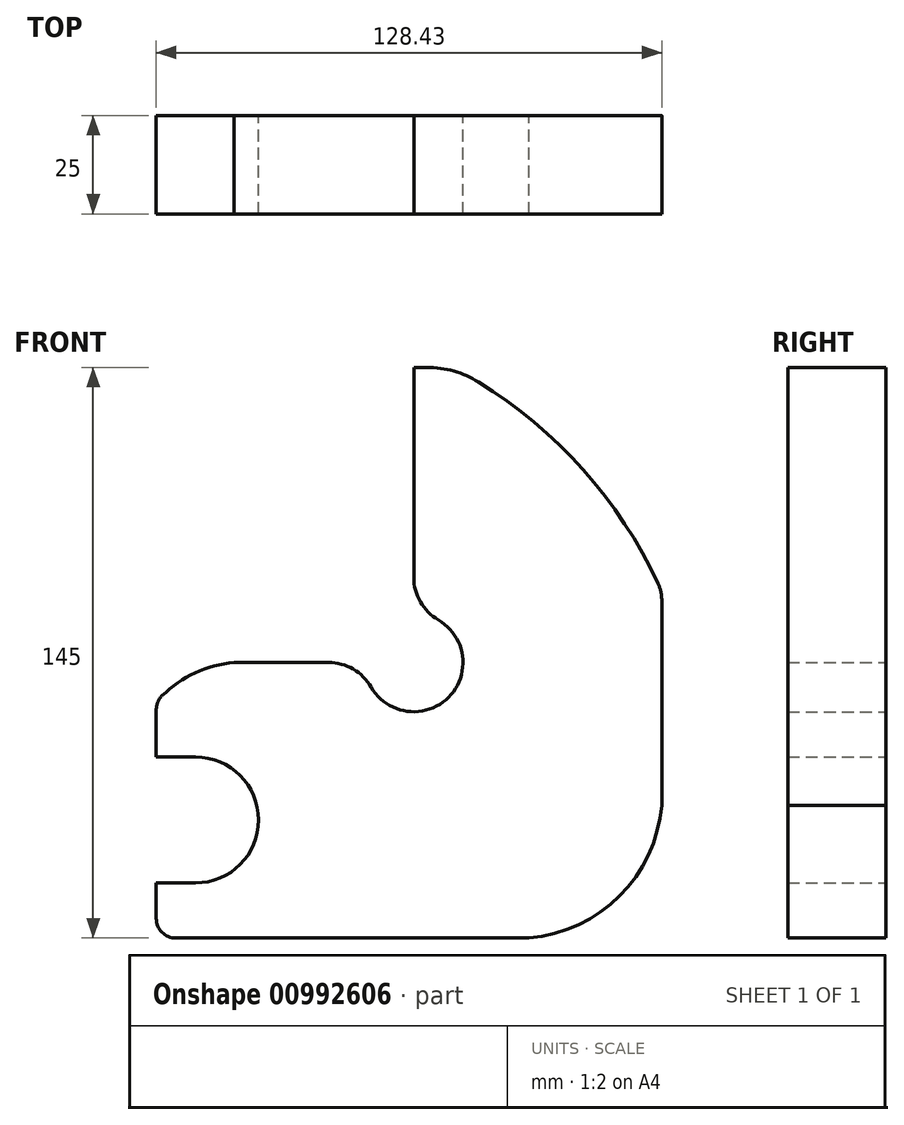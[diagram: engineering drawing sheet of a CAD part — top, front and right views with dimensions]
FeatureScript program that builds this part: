
annotation { "Feature Type Name" : "Feature", "Feature Type Description" : "" }
export const myFeature = defineFeature(function(context is Context, id is Id, definition is map)
    precondition{}
    {
        {
            var Q0;
            Q0=qCreatedBy(makeId("Front.planeOp"),FACE);
            var sketch = newSketch(context, id + "F0", { "sketchPlane" : qUnion([Q0])});
            skLineSegment(sketch, "E0", {"start": v(0, 0) * mm, "end": v(65.43, 0) * mm});
            skLineSegment(sketch, "E1", {"start": v(65.43, 0) * mm, "end": v(65.43, 75) * mm});
            skLineSegment(sketch, "E2", {"start": v(65.43, 75) * mm, "end": v(128.43, 75) * mm});
            skLineSegment(sketch, "E3", {"start": v(128.43, 75) * mm, "end": v(128.43, -70) * mm});
            skLineSegment(sketch, "E4", {"start": v(128.43, -70) * mm, "end": v(0, -70) * mm});
            skLineSegment(sketch, "E5", {"start": v(0, -70) * mm, "end": v(0, -56) * mm});
            skLineSegment(sketch, "E6", {"start": v(0, -24) * mm, "end": v(0, 0) * mm});
            skPoint(sketch, "E7", {"position": v(75.43, 75) * mm});
            skPoint(sketch, "E8", {"position": v(128.43, 18) * mm});
            skPoint(sketch, "E9", {"position": v(128.43, -30) * mm});
            skPoint(sketch, "E10", {"position": v(0, -10) * mm});
            skArc(sketch, "E11", {"start": v(128.43, 18) * mm, "mid": v(106.68, 50.92) * mm, "end": v(75.43, 75) * mm});
            skArc(sketch, "E12", {"start": v(88.43, -70) * mm, "mid": v(117.72, -59.3) * mm, "end": v(128.43, -30) * mm});
            skArc(sketch, "E13", {"start": v(25.22, 0) * mm, "mid": v(11.42, -1.99) * mm, "end": v(0, -10) * mm});
            skCircle(sketch, "E14", {"center": v(65.43, 0) * mm, "radius": 12.5 * mm});
            skCircle(sketch, "E15", {"center": v(10, -40) * mm, "radius": 16 * mm});
            skLineSegment(sketch, "E16", {"start": v(0, -56) * mm, "end": v(10, -56) * mm});
            skLineSegment(sketch, "E17", {"start": v(0, -24) * mm, "end": v(10, -24) * mm});
            skSolve(sketch);
        }
        {
            var Q0;
            {var subQ0=sQuery(id+"F0.wireOp",EDGE,"E5");Q0=makeQuery(id+"F0.imprint","IMPRINT",FACE,{"disambiguationData":[TD([[makeQuery(id+"F0.imprint","IMPRINT",EDGE,{"derivedFrom":subQ0}),-1.0]])]});}
            extrude(context, id + "F1", {"entities" : qUnion([Q0]), "depth" : 25 * mm, "offsetDistance" : 25 * mm});
        }
        {
            var Q0;
            Q0=makeQuery(id+"F1.opExtrude","SWEPT_EDGE",EDGE,{"disambiguationData":[OSD([sQuery(id+"F0.wireOp",EDGE,"E1"),sQuery(id+"F0.wireOp",EDGE,"E14")])]});
            fillet(context, id + "F2", {"entities" : qUnion([Q0]), "radius" : 12.5 * mm, "tangentPropagation" : true, "allowEdgeOverflow" : false});
        }
        {
            var Q0;
            Q0=makeQuery(id+"F1.opExtrude","SWEPT_EDGE",EDGE,{"disambiguationData":[OSD([sQuery(id+"F0.wireOp",EDGE,"E0"),sQuery(id+"F0.wireOp",EDGE,"E14")])]});
            fillet(context, id + "F3", {"entities" : qUnion([Q0]), "radius" : 12.5 * mm, "tangentPropagation" : true, "allowEdgeOverflow" : false});
        }
        {
            var Q0;
            Q0=makeQuery(id+"F1.opExtrude","SWEPT_EDGE",EDGE,{"disambiguationData":[OSD([sQuery(id+"F0.wireOp",EDGE,"E2"),sQuery(id+"F0.wireOp",EDGE,"E11")])]});
            fillet(context, id + "F4", {"entities" : qUnion([Q0]), "radius" : 25 * mm, "tangentPropagation" : true, "allowEdgeOverflow" : false});
        }
        {
            var Q0;
            Q0=makeQuery(id+"F1.opExtrude","SWEPT_EDGE",EDGE,{"disambiguationData":[OSD([sQuery(id+"F0.wireOp",EDGE,"E6"),sQuery(id+"F0.wireOp",EDGE,"E13")])]});
            fillet(context, id + "F5", {"entities" : qUnion([Q0]), "radius" : 5 * mm, "tangentPropagation" : true, "allowEdgeOverflow" : false});
        }
        {
            var Q0;
            Q0=makeQuery(id+"F1.opExtrude","SWEPT_EDGE",EDGE,{"disambiguationData":[OSD([sQuery(id+"F0.wireOp",EDGE,"E4"),sQuery(id+"F0.wireOp",EDGE,"E5")])]});
            fillet(context, id + "F6", {"entities" : qUnion([Q0]), "radius" : 5 * mm, "tangentPropagation" : true, "allowEdgeOverflow" : false});
        }
        {
            var Q0;
            Q0=makeQuery(id+"F1.opExtrude","SWEPT_EDGE",EDGE,{"disambiguationData":[OSD([sQuery(id+"F0.wireOp",EDGE,"E3"),sQuery(id+"F0.wireOp",EDGE,"E11")])]});
            fillet(context, id + "F7", {"entities" : qUnion([Q0]), "radius" : 10 * mm, "tangentPropagation" : true, "allowEdgeOverflow" : false});
        }
    });
